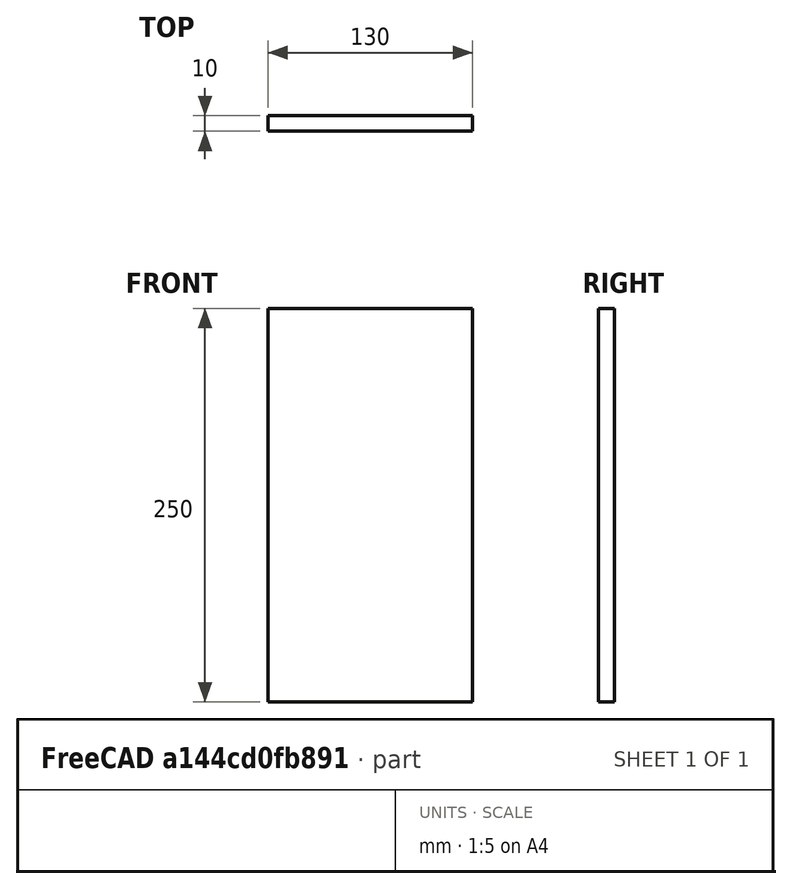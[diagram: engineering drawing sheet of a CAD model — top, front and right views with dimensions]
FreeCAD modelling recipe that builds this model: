
FCSTD DOCUMENT  (FreeCAD 0.21R33771 (Git))
Label: PiastraContropunta
License: All rights reserved
LicenseURL: http://en.wikipedia.org/wiki/All_rights_reserved
objects: Sketcher::SketchObject×3, PartDesign::CoordinateSystem×1, PartDesign::Pad×1, PartDesign::Body×1
note: 7 computed .brp shape members not serialized (recipe doc carries the construction recipe); baked Part::Feature solids carry a one-line shape summary decoded from their .brp

FEATURE [Sketcher::SketchObject] Sketch
  FullyConstrained = true
  MapMode = 5
  Placement = pos=(0,0,0) rot=(1,0,0;1.5708rad)
  Support = -> [XZ_Plane]
  sketch-geometry (4):
    g0: LineSegment StartX=0 StartY=0 StartZ=0 EndX=130 EndY=0 EndZ=0
    g1: LineSegment StartX=130 StartY=0 StartZ=0 EndX=130 EndY=250 EndZ=0
    g2: LineSegment StartX=130 StartY=250 StartZ=0 EndX=0 EndY=250 EndZ=0
    g3: LineSegment StartX=0 StartY=250 StartZ=0 EndX=0 EndY=0 EndZ=0
  constraints (11):
    c: Coincident(g0,g1)
    c: Coincident(g1,g2)
    c: Coincident(g2,g3)
    c: Coincident(g3,g0)
    c: Horizontal(g0)
    c: Horizontal(g2)
    c: Vertical(g1)
    c: Vertical(g3)
    c: Coincident(g0,g-1)
    c: DistanceX(g0,g0) = 130
    c: DistanceY(g3,g3) = 250
FEATURE [Sketcher::SketchObject] Sketch001
  FullyConstrained = true
  MapMode = 5
  Placement = pos=(0,-10,0) rot=(1,0,0;1.5708rad)
  sketch-geometry (31):
    g0: Circle CenterX=5 CenterY=235 CenterZ=0 NormalX=0 NormalY=0 NormalZ=1 AngleXU=0 Radius=2.1
    g1: Circle CenterX=41 CenterY=235 CenterZ=0 NormalX=0 NormalY=0 NormalZ=1 AngleXU=0 Radius=2.1
    g2: LineSegment StartX=5 StartY=235 StartZ=0 EndX=41 EndY=235 EndZ=0
    g3: Circle CenterX=5 CenterY=203 CenterZ=0 NormalX=0 NormalY=0 NormalZ=1 AngleXU=0 Radius=2.1
    g4: LineSegment StartX=5 StartY=235 StartZ=0 EndX=5 EndY=203 EndZ=0
    g5: Circle CenterX=41 CenterY=203 CenterZ=0 NormalX=0 NormalY=0 NormalZ=1 AngleXU=0 Radius=2.1
    g6: LineSegment StartX=5 StartY=203 StartZ=0 EndX=41 EndY=203 EndZ=0
    g7: Circle CenterX=90 CenterY=235 CenterZ=0 NormalX=0 NormalY=0 NormalZ=1 AngleXU=0 Radius=2.1
    g8: Circle CenterX=126 CenterY=235 CenterZ=0 NormalX=0 NormalY=0 NormalZ=1 AngleXU=0 Radius=2.1
    g9: LineSegment StartX=90 StartY=235 StartZ=0 EndX=126 EndY=235 EndZ=0
    g10: Circle CenterX=90 CenterY=203 CenterZ=0 NormalX=0 NormalY=0 NormalZ=1 AngleXU=0 Radius=2.1
    g11: LineSegment StartX=90 StartY=235 StartZ=0 EndX=90 EndY=203 EndZ=0
    g12: Circle CenterX=126 CenterY=203 CenterZ=0 NormalX=0 NormalY=0 NormalZ=1 AngleXU=0 Radius=2.1
    g13: LineSegment StartX=90 StartY=203 StartZ=0 EndX=126 EndY=203 EndZ=0
    g14: LineSegment StartX=5 StartY=235 StartZ=0 EndX=90 EndY=235 EndZ=0
    g15: Circle CenterX=5 CenterY=45 CenterZ=0 NormalX=0 NormalY=0 NormalZ=1 AngleXU=0 Radius=2.1
    g16: Circle CenterX=41 CenterY=45 CenterZ=0 NormalX=0 NormalY=0 NormalZ=1 AngleXU=0 Radius=2.1
    g17: LineSegment StartX=5 StartY=45 StartZ=0 EndX=41 EndY=45 EndZ=0
    g18: Circle CenterX=5 CenterY=13 CenterZ=0 NormalX=0 NormalY=0 NormalZ=1 AngleXU=0 Radius=2.1
    g19: LineSegment StartX=5 StartY=45 StartZ=0 EndX=5 EndY=13 EndZ=0
    g20: Circle CenterX=41 CenterY=13 CenterZ=0 NormalX=0 NormalY=0 NormalZ=1 AngleXU=0 Radius=2.1
    g21: LineSegment StartX=5 StartY=13 StartZ=0 EndX=41 EndY=13 EndZ=0
    g22: LineSegment StartX=5 StartY=235 StartZ=0 EndX=5 EndY=45 EndZ=0
    g23: Circle CenterX=90 CenterY=45 CenterZ=0 NormalX=0 NormalY=0 NormalZ=1 AngleXU=0 Radius=2.1
    g24: Circle CenterX=126 CenterY=45 CenterZ=0 NormalX=0 NormalY=0 NormalZ=1 AngleXU=0 Radius=2.1
    g25: LineSegment StartX=90 StartY=45 StartZ=0 EndX=126 EndY=45 EndZ=0
    g26: Circle CenterX=90 CenterY=13 CenterZ=0 NormalX=0 NormalY=0 NormalZ=1 AngleXU=0 Radius=2.1
    g27: LineSegment StartX=90 StartY=45 StartZ=0 EndX=90 EndY=13 EndZ=0
    g28: Circle CenterX=126 CenterY=13 CenterZ=0 NormalX=0 NormalY=0 NormalZ=1 AngleXU=0 Radius=2.1
    g29: LineSegment StartX=90 StartY=13 StartZ=0 EndX=126 EndY=13 EndZ=0
    g30: LineSegment StartX=5 StartY=45 StartZ=0 EndX=90 EndY=45 EndZ=0
  constraints (78):
    c: Coincident(g0,g2)
    c: Coincident(g1,g2)
    c: Distance(g2) = 36
    c: Angle(g2) = 0
    c: Coincident(g0,g4)
    c: Coincident(g3,g4)
    c: Distance(g4) = 32
    c: Perpendicular(g4,g2)
    c: Coincident(g3,g6)
    c: Coincident(g5,g6)
    c: Equal(g2,g6)
    c: Parallel(g6,g2)
    c: Coincident(g7,g9)
    c: Coincident(g8,g9)
    c: Distance(g9) = 36
    c: Angle(g9) = 0
    c: Coincident(g7,g11)
    c: Coincident(g10,g11)
    c: Distance(g11) = 32
    c: Perpendicular(g11,g9)
    c: Coincident(g10,g13)
    c: Coincident(g12,g13)
    c: Equal(g9,g13)
    c: Parallel(g13,g9)
    c: Coincident(g0,g14)
    c: Coincident(g7,g14)
    c: Distance(g14) = 85
    c: Angle(g14) = 0
    c: Coincident(g15,g17)
    c: Coincident(g16,g17)
    c: Distance(g17) = 36
    c: Angle(g17) = 0
    c: Coincident(g15,g19)
    c: Coincident(g18,g19)
    c: Distance(g19) = 32
    c: Perpendicular(g19,g17)
    c: Coincident(g18,g21)
    c: Coincident(g20,g21)
    c: Equal(g17,g21)
    c: Parallel(g21,g17)
    c: Coincident(g0,g22)
    c: Coincident(g15,g22)
    c: Distance(g22) = 190
    c: Perpendicular(g22,g14)
    c: Coincident(g23,g25)
    c: Coincident(g24,g25)
    c: Distance(g25) = 36
    c: Angle(g25) = 0
    c: Coincident(g23,g27)
    c: Coincident(g26,g27)
    c: Perpendicular(g27,g25)
    c: Coincident(g26,g29)
    c: Coincident(g28,g29)
    c: Equal(g25,g29)
    c: Parallel(g29,g25)
    c: Coincident(g15,g30)
    c: Coincident(g23,g30)
    c: Equal(g14,g30)
    c: Parallel(g30,g14)
    c: DistanceY(g-1,g0) = 235
    c: DistanceX(g-1,g0) = 5
    c: Radius(g0) = 2.1
    c: Equal(g3,g0)
    c: Equal(g0,g1)
    c: Equal(g1,g5)
    c: Equal(g5,g10)
    c: Equal(g10,g12)
    c: Equal(g12,g8)
    c: Equal(g8,g7)
    c: Equal(g16,g23)
    c: Equal(g23,g24)
    c: Equal(g24,g18)
    c: Equal(g18,g20)
    c: Equal(g15,g16)
    c: Equal(g24,g28)
    c: Equal(g28,g26)
    c: Equal(g27,g19)
    c: Equal(g3,g15)
FEATURE [Sketcher::SketchObject] Sketch002
  FullyConstrained = false
  MapMode = 5
  Placement = pos=(0,-10,0) rot=(1,0,0;1.5708rad)
  sketch-geometry (15):
    g0: Circle CenterX=15 CenterY=280 CenterZ=0 NormalX=0 NormalY=0 NormalZ=1 AngleXU=0 Radius=4
    g1: Circle CenterX=5 CenterY=13 CenterZ=0 NormalX=0 NormalY=0 NormalZ=1 AngleXU=0 Radius=4
    g2: Circle CenterX=5 CenterY=45 CenterZ=0 NormalX=0 NormalY=0 NormalZ=1 AngleXU=0 Radius=4
    g3: LineSegment StartX=5 StartY=13 StartZ=0 EndX=5 EndY=45 EndZ=0
    g4: Circle CenterX=41 CenterY=13 CenterZ=0 NormalX=0 NormalY=0 NormalZ=1 AngleXU=0 Radius=4
    g5: LineSegment StartX=5 StartY=13 StartZ=0 EndX=41 EndY=13 EndZ=0
    g6: Circle CenterX=41 CenterY=45 CenterZ=0 NormalX=0 NormalY=0 NormalZ=1 AngleXU=0 Radius=4
    g7: LineSegment StartX=41 StartY=13 StartZ=0 EndX=41 EndY=45 EndZ=0
    g8: Circle CenterX=90 CenterY=13 CenterZ=0 NormalX=0 NormalY=0 NormalZ=1 AngleXU=0 Radius=4
    g9: Circle CenterX=90 CenterY=45 CenterZ=0 NormalX=0 NormalY=0 NormalZ=1 AngleXU=0 Radius=4
    g10: LineSegment StartX=90 StartY=13 StartZ=0 EndX=90 EndY=45 EndZ=0
    g11: Circle CenterX=126 CenterY=13 CenterZ=0 NormalX=0 NormalY=0 NormalZ=1 AngleXU=0 Radius=4
    g12: LineSegment StartX=90 StartY=13 StartZ=0 EndX=126 EndY=13 EndZ=0
    g13: Circle CenterX=126 CenterY=45 CenterZ=0 NormalX=0 NormalY=0 NormalZ=1 AngleXU=0 Radius=4
    g14: LineSegment StartX=126 StartY=13 StartZ=0 EndX=126 EndY=45 EndZ=0
  constraints (36):
    c: DistanceY(g-1,g1) = 13
    c: DistanceX(g-1,g1) = 5
    c: Radius(g1) = 4
    c: Radius(g2) = 4
    c: Coincident(g1,g3)
    c: Coincident(g2,g3)
    c: Distance(g3) = 32
    c: Angle(g3) = 1.5708
    c: Radius(g4) = 4
    c: Coincident(g1,g5)
    c: Coincident(g4,g5)
    c: Distance(g5) = 36
    c: Perpendicular(g5,g3)
    c: Radius(g6) = 4
    c: Coincident(g4,g7)
    c: Coincident(g6,g7)
    c: Equal(g3,g7)
    c: Parallel(g7,g3)
    c: DistanceY(g-1,g8) = 13
    c: Radius(g8) = 4
    c: Radius(g9) = 4
    c: Coincident(g8,g10)
    c: Coincident(g9,g10)
    c: Distance(g10) = 32
    c: Angle(g10) = 1.5708
    c: Radius(g11) = 4
    c: Coincident(g8,g12)
    c: Coincident(g11,g12)
    c: Distance(g12) = 36
    c: Perpendicular(g12,g10)
    c: Radius(g13) = 4
    c: Coincident(g11,g14)
    c: Coincident(g13,g14)
    c: Equal(g10,g14)
    c: Parallel(g14,g10)
    c: DistanceX(g1,g8) = 85
FEATURE [PartDesign::CoordinateSystem] LCS_PiastraContropunta
  AttacherType = Attacher::AttachEngine3D
FEATURE [PartDesign::Pad] Pad
  Direction = (0,-1,-2e-16)
  Length = 10
  Length2 = 10
  Placement = pos=(0,0,0) rot=(1,0,0;1.5708rad)
  Profile = -> Sketch
  ReferenceAxis = -> Sketch [N_Axis]
  Type = 0
FEATURE [PartDesign::Body] Body
  Group = -> [Sketch,Sketch001,Sketch002,LCS_PiastraContropunta,Pad]
  Origin = -> Origin
  Tip = -> Pad
